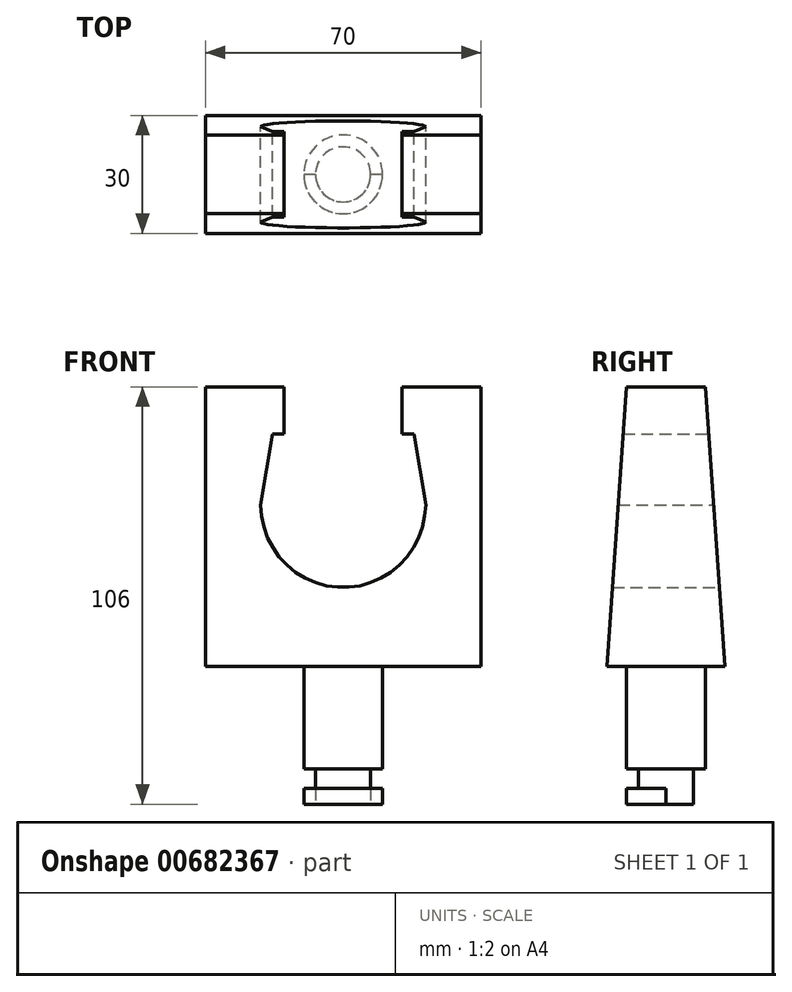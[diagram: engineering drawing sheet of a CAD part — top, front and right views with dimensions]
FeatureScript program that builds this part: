
annotation { "Feature Type Name" : "Feature", "Feature Type Description" : "" }
export const myFeature = defineFeature(function(context is Context, id is Id, definition is map)
    precondition{}
    {
        {
            var Q0;
            Q0=qCreatedBy(makeId("Front.planeOp"),FACE);
            var sketch = newSketch(context, id + "F0", { "sketchPlane" : qUnion([Q0])});
            skLineSegment(sketch, "E0.bottom", {"start": v(-35, 0) * mm, "end": v(35, 0) * mm});
            skLineSegment(sketch, "E0.top", {"start": v(-35, 71) * mm, "end": v(-15, 71) * mm});
            skLineSegment(sketch, "E0.left", {"start": v(-35, 0) * mm, "end": v(-35, 71) * mm});
            skLineSegment(sketch, "E0.right", {"start": v(35, 0) * mm, "end": v(35, 71) * mm});
            skArc(sketch, "E1", {"start": v(-21, 41) * mm, "mid": v(0, 20) * mm, "end": v(21, 41) * mm});
            skLineSegment(sketch, "E2.left", {"start": v(-15, 71) * mm, "end": v(-15, 59) * mm});
            skLineSegment(sketch, "E2.right", {"start": v(15, 71) * mm, "end": v(15, 59) * mm});
            skLineSegment(sketch, "E3.trimOffspring", {"start": v(15, 71) * mm, "end": v(35, 71) * mm});
            skLineSegment(sketch, "E4", {"start": v(-15, 59) * mm, "end": v(-18, 59) * mm});
            skLineSegment(sketch, "E5", {"start": v(-18, 59) * mm, "end": v(-21, 41) * mm});
            skLineSegment(sketch, "E6", {"start": v(15, 59) * mm, "end": v(18, 59) * mm});
            skLineSegment(sketch, "E7", {"start": v(18, 59) * mm, "end": v(21, 41) * mm});
            skSolve(sketch);
        }
        {
            var Q0;
            Q0=makeQuery(id+"F0.imprint","IMPRINT",FACE,{"disambiguationData":[TD([[makeQuery(id+"F0.imprint","IMPRINT",EDGE,{"derivedFrom":sQuery(id+"F0.wireOp",EDGE,"E0.bottom")}),1.0]])]});
            extrude(context, id + "F1", {"entities" : qUnion([Q0]), "endBound" : BoundingType.SYMMETRIC, "depth" : 30 * mm, "offsetDistance" : 25 * mm});
        }
        {
            var Q0;
            Q0=makeQuery(id+"F1.opExtrude","SWEPT_FACE",FACE,{"disambiguationData":[OSD([sQuery(id+"F0.wireOp",EDGE,"E0.left")])]});
            var sketch = newSketch(context, id + "F2", { "sketchPlane" : qUnion([Q0])});
            skLineSegment(sketch, "E8", {"start": v(-15, 71) * mm, "end": v(-15, 0) * mm});
            skLineSegment(sketch, "E9", {"start": v(-15, 0) * mm, "end": v(-10, 71) * mm});
            skLineSegment(sketch, "E10", {"start": v(-10, 71) * mm, "end": v(-15, 71) * mm});
            skLineSegment(sketch, "E11.MirrorCS", {"start": v(15, 0) * mm, "end": v(10, 71) * mm});
            skLineSegment(sketch, "E12.MirrorCS", {"start": v(15, 71) * mm, "end": v(15, 0) * mm});
            skLineSegment(sketch, "E13.MirrorCS", {"start": v(10, 71) * mm, "end": v(15, 71) * mm});
            skSolve(sketch);
        }
        {
            var Q0;
            Q0 = qSketchRegion(id + "F2", true);
            extrude(context, id + "F3", {"entities" : qUnion([Q0]), "operationType" : NewBodyOperationType.REMOVE, "endBound" : BoundingType.THROUGH_ALL, "oppositeDirection" : true, "depth" : 25 * mm, "offsetDistance" : 25 * mm});
        }
        {
            var Q0;
            Q0=qCreatedBy(makeId("Front.planeOp"),FACE);
            var sketch = newSketch(context, id + "F4", { "sketchPlane" : qUnion([Q0])});
            skLineSegment(sketch, "E14", {"start": v(0, 0) * mm, "end": v(0, -35) * mm});
            skLineSegment(sketch, "E15", {"start": v(0, -35) * mm, "end": v(10, -35) * mm});
            skLineSegment(sketch, "E16", {"start": v(10, -35) * mm, "end": v(10, -31) * mm});
            skLineSegment(sketch, "E17", {"start": v(10, -31) * mm, "end": v(7, -31) * mm});
            skLineSegment(sketch, "E18", {"start": v(7, -31) * mm, "end": v(7, -26) * mm});
            skLineSegment(sketch, "E19", {"start": v(7, -26) * mm, "end": v(10, -26) * mm});
            skLineSegment(sketch, "E20", {"start": v(10, -26) * mm, "end": v(10, 0) * mm});
            skLineSegment(sketch, "E21", {"start": v(10, 0) * mm, "end": v(0, 0) * mm});
            skSolve(sketch);
        }
        {
            var Q0;
            Q0 = qSketchRegion(id + "F4", true);
            var Q1;
            Q1=sQuery(id+"F4.wireOp",EDGE,"E14");
            revolve(context, id + "F5", {"operationType" : NewBodyOperationType.ADD, "entities" : qUnion([Q0]), "axis" : qUnion([Q1]), "revolveType" : RevolveType.FULL});
        }
        {
            var Q0;
            Q0=makeQuery(id+"F5.opRevolve","SWEPT_FACE",FACE,{"disambiguationData":[OSD([sQuery(id+"F4.wireOp",EDGE,"E15")])]});
            var sketch = newSketch(context, id + "F6", { "sketchPlane" : qUnion([Q0])});
            skArc(sketch, "E22", {"start": v(7, 0) * mm, "mid": v(0, -7) * mm, "end": v(-7, 0) * mm});
            skLineSegment(sketch, "E23", {"start": v(-7, 0) * mm, "end": v(-17, 0) * mm});
            skLineSegment(sketch, "E24", {"start": v(-17, 0) * mm, "end": v(-17, -26) * mm});
            skLineSegment(sketch, "E25", {"start": v(-17, -26) * mm, "end": v(17, -26) * mm});
            skLineSegment(sketch, "E26", {"start": v(17, -26) * mm, "end": v(17, 0) * mm});
            skLineSegment(sketch, "E27", {"start": v(17, 0) * mm, "end": v(7, 0) * mm});
            skSolve(sketch);
        }
        {
            var Q0;
            Q0 = qSketchRegion(id + "F6", true);
            var Q1;
            Q1=makeQuery(id+"F5.opRevolve","SWEPT_FACE",FACE,{"disambiguationData":[OSD([sQuery(id+"F4.wireOp",EDGE,"E19")])]});
            extrude(context, id + "F7", {"entities" : qUnion([Q0]), "operationType" : NewBodyOperationType.REMOVE, "oppositeDirection" : true, "depth" : 6 * mm, "endBoundEntityFace" : qUnion([Q1]), "offsetDistance" : 25 * mm});
        }
    });
